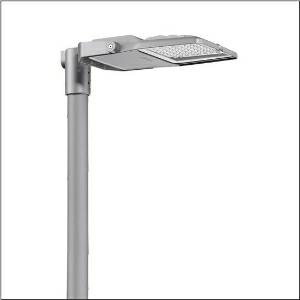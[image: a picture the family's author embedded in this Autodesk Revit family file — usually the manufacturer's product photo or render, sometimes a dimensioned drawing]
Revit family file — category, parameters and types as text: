
# Revit family: floodlight_fl_21_mini___pl52_5xa7772c2d3a_a18d
name_source: partatom
category: Lighting Fixtures
units: mm (PartAtom-declared; Revit-internal decimal feet)

## family parameters
Cut with Voids When Loaded = No
Host = Face
Light Source = No
Part Type = Normal
Room Calculation Point = No
Round Connector Dimension = Use Diameter
Shared = No

## types (1)
- --- (1 x LED, 12210 lm, 87.2 W, 3000K)
    Apparent Load = 87 VA
    CIE Flux Codes = 26 60 98 100 100
    Color Rendering = 70
    Color Temperature = 3000K
    Default Elevation = 1800 mm
    Description = Floodlight FL 21 mini, floodlight, primary light control with lens, of PMMA, primary optical cover: protective disc, of toughened safety glass, transparent, light distribution: PL52, light emission: direct distribution, installation type: surface-mounted, LED, High Power LED, rated luminous flux: 12.210lm, luminous efficacy: 140lm/W, light colour: 730, colour temperature: 3000K, control gear: ECG iQ, control: Auto-Match, Temp-Guard, Night-Set, Smart-Wire, Desk-Remote (wireless, voltage-free reading and setting of iQ features in the workshop via application-optimized NFC function/RFID function), optimised constant luminous flux control (CLO 2.0), Light-Fading, Lumen-Switch, with terminal, 6-pole, mains connection: 220..240V, AC, 50/60Hz, start of lifetime: 87W, end of lifetime: 92W, reduction: 40W, luminaire housing, of diecast aluminium, powder-coated, Siteco® metallic grey (DB 702S), corrosivity category C5 according to DIN EN ISO 12944, mast bracket, of steel, galvanised, powder-coated, protection rating (complete): IP66, insulation class (complete): insulation class II (safety insulation), certification: CE, ENEC, VDE, protection symbol: D, impact resistance: IK08, permissible operating ambient temperature: -40..+40°C, permissible operating ambient temperature for outdoor applications: -40..+50°C, standard: DIN EN 12944, packaging unit: 1 piece

Light Distribution: PL52
    Height = 70 mm
    Lamp = 1 x LED
    Lamp Light Flux = 12210 lm
    Lamp Power = 87.2 W
    Lamp count = 1
    Length = 485 mm
    Luminous efficacy = 140 lm/W
    Manufacturer = Siteco
    ModVariant = No
    Model = 5XA7772C2D3A
    Number of Poles = 1
    OnlyDefault = Yes
    Power Factor = 1
    Product Name = Floodlight FL 21 mini | PL52
    Product group = floodlight | pylon top
    ProductGroupID = 6101
    Protection Class = Protection class II
    Protection Degree = IP 66
    RLX_Detail_Level = 1
    RlxData = <blob elided: 101373 chars, md5=de01823d>
    Socket = socket
    Standby Power = 0 W
    System Light Flux = 12210 lm
    System Power = 87 W
    Type Comments = factory setting: luminous flux: 100 % | dim-lin: 254 | 456 mA
    Type Image = l_1007125.jpg
    URL = http://relux.com
    VarID = @adj_075423
    Voltage = 0 V
    Weight = 0.00 kg
    Width = 337 mm

## geometry (parser evidence)
native form markers: Blend x4, Sweep x11
no freeform markers — native parametric forms only
